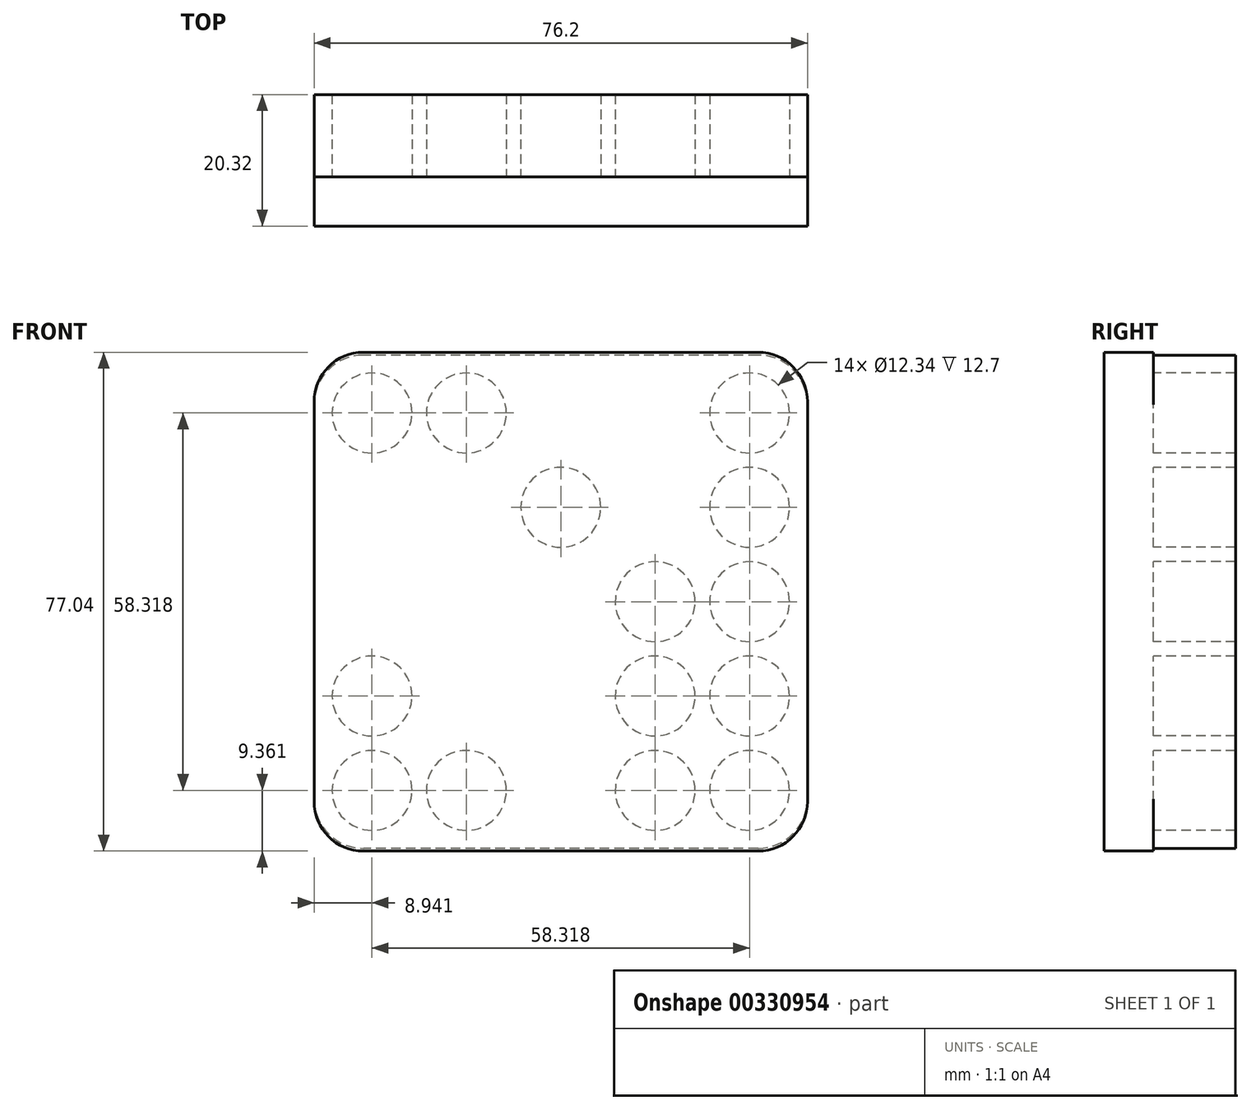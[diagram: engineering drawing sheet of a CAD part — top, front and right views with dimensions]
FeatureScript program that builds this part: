
annotation { "Feature Type Name" : "Feature", "Feature Type Description" : "" }
export const myFeature = defineFeature(function(context is Context, id is Id, definition is map)
    precondition{}
    {
        {
            var Q0;
            Q0=qCreatedBy(makeId("Front.planeOp"),FACE);
            var sketch = newSketch(context, id + "F0", { "sketchPlane" : qUnion([Q0])});
            skLineSegment(sketch, "E0.bottom", {"start": v(38.1, -38.1) * mm, "end": v(-38.1, -38.1) * mm});
            skLineSegment(sketch, "E0.top", {"start": v(38.1, 38.1) * mm, "end": v(-38.1, 38.1) * mm});
            skLineSegment(sketch, "E0.left", {"start": v(38.1, -38.1) * mm, "end": v(38.1, 38.1) * mm});
            skLineSegment(sketch, "E0.right", {"start": v(-38.1, -38.1) * mm, "end": v(-38.1, 38.1) * mm});
            skPoint(sketch, "E0.middle", {"position": v(0, 0) * mm});
            skLineSegment(sketch, "E1.left", {"start": v(38.1, -38.1) * mm, "end": v(38.1, -30.48) * mm});
            skSolve(sketch);
        }
        {
            var Q0;
            Q0=qSketchRegion(id+"F0",true);
            extrude(context, id + "F1", {"entities" : qUnion([Q0]), "depth" : 12.7 * mm});
        }
        {
            var Q0;
            Q0=makeQuery(id+"F1.opExtrude","CAP_FACE",FACE,{"disambiguationData":[OSD([sQuery(id+"F0.wireOp",EDGE,"E0.bottom"),sQuery(id+"F0.wireOp",EDGE,"E0.top"),sQuery(id+"F0.wireOp",EDGE,"E0.left"),sQuery(id+"F0.wireOp",EDGE,"E0.right"),sQuery(id+"F0.wireOp",EDGE,"jwXeI2Gn-2uBu-UpR7-ZfaP-BlmGfNdsuJBv.bottom"),sQuery(id+"F0.wireOp",EDGE,"jwXeI2Gn-2uBu-UpR7-ZfaP-BlmGfNdsuJBv.top"),sQuery(id+"F0.wireOp",EDGE,"jwXeI2Gn-2uBu-UpR7-ZfaP-BlmGfNdsuJBv.right"),sQuery(id+"F0.wireOp",EDGE,"E1.bottom"),sQuery(id+"F0.wireOp",EDGE,"E1.top"),sQuery(id+"F0.wireOp",EDGE,"E1.right"),sQuery(id+"F0.wireOp",EDGE,"Ah4uGkzg-DGqc-S60Q-QTGu-lLs24q3gFamp.bottom"),sQuery(id+"F0.wireOp",EDGE,"Ah4uGkzg-DGqc-S60Q-QTGu-lLs24q3gFamp.left"),sQuery(id+"F0.wireOp",EDGE,"Ah4uGkzg-DGqc-S60Q-QTGu-lLs24q3gFamp.right")])],"isStart":false});
            var sketch = newSketch(context, id + "F2", { "sketchPlane" : qUnion([Q0])});
            skLineSegment(sketch, "E2.bottom", {"start": v(0, 0) * mm, "end": v(14.58, 0) * mm});
            skLineSegment(sketch, "E2.top", {"start": v(0, 14.58) * mm, "end": v(14.58, 14.58) * mm});
            skLineSegment(sketch, "E2.left", {"start": v(0, 0) * mm, "end": v(0, 14.58) * mm});
            skLineSegment(sketch, "E2.right", {"start": v(14.58, 0) * mm, "end": v(14.58, 14.58) * mm});
            skLineSegment(sketch, "E3.top", {"start": v(0, 29.16) * mm, "end": v(14.58, 29.16) * mm});
            skLineSegment(sketch, "E3.left", {"start": v(0, 14.58) * mm, "end": v(0, 29.16) * mm});
            skLineSegment(sketch, "E3.right", {"start": v(14.58, 14.58) * mm, "end": v(14.58, 29.16) * mm});
            skLineSegment(sketch, "E4.top", {"start": v(0, -14.58) * mm, "end": v(14.58, -14.58) * mm});
            skLineSegment(sketch, "E4.left", {"start": v(0, 0) * mm, "end": v(0, -14.58) * mm});
            skLineSegment(sketch, "E4.right", {"start": v(14.58, 0) * mm, "end": v(14.58, -14.58) * mm});
            skLineSegment(sketch, "E5.bottom", {"start": v(0, 0) * mm, "end": v(-14.58, 0) * mm});
            skLineSegment(sketch, "E5.top", {"start": v(0, -14.58) * mm, "end": v(-14.58, -14.58) * mm});
            skLineSegment(sketch, "E5.right", {"start": v(-14.58, 0) * mm, "end": v(-14.58, -14.58) * mm});
            skLineSegment(sketch, "E6.bottom", {"start": v(0, 14.58) * mm, "end": v(-14.58, 14.58) * mm});
            skLineSegment(sketch, "E6.left", {"start": v(0, 14.58) * mm, "end": v(0, 0) * mm});
            skLineSegment(sketch, "E6.right", {"start": v(-14.58, 14.58) * mm, "end": v(-14.58, 0) * mm});
            skLineSegment(sketch, "E7.top", {"start": v(0, 29.16) * mm, "end": v(-14.58, 29.16) * mm});
            skLineSegment(sketch, "E7.right", {"start": v(-14.58, 14.58) * mm, "end": v(-14.58, 29.16) * mm});
            skLineSegment(sketch, "E8.bottom", {"start": v(-14.58, 14.58) * mm, "end": v(-29.16, 14.58) * mm});
            skLineSegment(sketch, "E8.top", {"start": v(-14.58, 29.16) * mm, "end": v(-29.16, 29.16) * mm});
            skLineSegment(sketch, "E8.right", {"start": v(-29.16, 14.58) * mm, "end": v(-29.16, 29.16) * mm});
            skLineSegment(sketch, "E9.top", {"start": v(-14.58, 0) * mm, "end": v(-29.16, 0) * mm});
            skLineSegment(sketch, "E9.right", {"start": v(-29.16, 14.58) * mm, "end": v(-29.16, 0) * mm});
            skLineSegment(sketch, "E10.bottom", {"start": v(-14.58, -14.58) * mm, "end": v(-29.16, -14.58) * mm});
            skLineSegment(sketch, "E10.left", {"start": v(-14.58, -14.58) * mm, "end": v(-14.58, 0) * mm});
            skLineSegment(sketch, "E10.right", {"start": v(-29.16, -14.58) * mm, "end": v(-29.16, 0) * mm});
            skLineSegment(sketch, "E11.bottom", {"start": v(14.58, -14.58) * mm, "end": v(29.16, -14.58) * mm});
            skLineSegment(sketch, "E11.top", {"start": v(14.58, 0) * mm, "end": v(29.16, 0) * mm});
            skLineSegment(sketch, "E11.left", {"start": v(14.58, -14.58) * mm, "end": v(14.58, 0) * mm});
            skLineSegment(sketch, "E11.right", {"start": v(29.16, -14.58) * mm, "end": v(29.16, 0) * mm});
            skLineSegment(sketch, "E12.top", {"start": v(14.58, 14.58) * mm, "end": v(29.16, 14.58) * mm});
            skLineSegment(sketch, "E12.right", {"start": v(29.16, 0) * mm, "end": v(29.16, 14.58) * mm});
            skLineSegment(sketch, "E13.top", {"start": v(14.58, 29.16) * mm, "end": v(29.16, 29.16) * mm});
            skLineSegment(sketch, "E13.right", {"start": v(29.16, 14.58) * mm, "end": v(29.16, 29.16) * mm});
            skLineSegment(sketch, "E14.top", {"start": v(14.58, -29.16) * mm, "end": v(29.16, -29.16) * mm});
            skLineSegment(sketch, "E14.left", {"start": v(14.58, -14.58) * mm, "end": v(14.58, -29.16) * mm});
            skLineSegment(sketch, "E14.right", {"start": v(29.16, -14.58) * mm, "end": v(29.16, -29.16) * mm});
            skLineSegment(sketch, "E15.bottom", {"start": v(14.58, -29.16) * mm, "end": v(0, -29.16) * mm});
            skLineSegment(sketch, "E15.top", {"start": v(14.58, -14.58) * mm, "end": v(0, -14.58) * mm});
            skLineSegment(sketch, "E15.left", {"start": v(14.58, -29.16) * mm, "end": v(14.58, -14.58) * mm});
            skLineSegment(sketch, "E15.right", {"start": v(0, -29.16) * mm, "end": v(0, -14.58) * mm});
            skLineSegment(sketch, "E16.bottom", {"start": v(0, -29.16) * mm, "end": v(-14.58, -29.16) * mm});
            skLineSegment(sketch, "E16.right", {"start": v(-14.58, -29.16) * mm, "end": v(-14.58, -14.58) * mm});
            skLineSegment(sketch, "E17.bottom", {"start": v(-14.58, -29.16) * mm, "end": v(-29.16, -29.16) * mm});
            skLineSegment(sketch, "E17.right", {"start": v(-29.16, -29.16) * mm, "end": v(-29.16, -14.58) * mm});
            skSolve(sketch);
        }
        {
            var Q0;
            Q0=sQuery(id+"F2.wireOp",VERTEX,"E8.top.end");
            var Q1;
            Q1=sQuery(id+"F2.wireOp",VERTEX,"E8.top.start");
            var Q2;
            Q2=sQuery(id+"F2.wireOp",VERTEX,"E3.left.end");
            var Q3;
            Q3=sQuery(id+"F2.wireOp",VERTEX,"E3.right.end");
            var Q4;
            Q4=sQuery(id+"F2.wireOp",VERTEX,"E13.right.end");
            var Q5;
            Q5=sQuery(id+"F2.wireOp",VERTEX,"E12.top.end");
            var Q6;
            Q6=sQuery(id+"F2.wireOp",VERTEX,"E11.right.end");
            var Q7;
            Q7=sQuery(id+"F2.wireOp",VERTEX,"E11.bottom.end");
            var Q8;
            Q8=sQuery(id+"F2.wireOp",VERTEX,"E14.top.end");
            var Q9;
            Q9=sQuery(id+"F2.wireOp",VERTEX,"E14.top.start");
            var Q10;
            Q10=sQuery(id+"F2.wireOp",VERTEX,"E14.left.start");
            var Q11;
            Q11=sQuery(id+"F2.wireOp",VERTEX,"E11.left.end");
            var Q12;
            Q12=sQuery(id+"F2.wireOp",VERTEX,"E2.top.end");
            var Q13;
            Q13=sQuery(id+"F2.wireOp",VERTEX,"E6.left.start");
            var Q14;
            Q14=sQuery(id+"F2.wireOp",VERTEX,"E2.bottom.start");
            var Q15;
            Q15=sQuery(id+"F2.wireOp",VERTEX,"E4.left.end");
            var Q16;
            Q16=sQuery(id+"F2.wireOp",VERTEX,"E15.right.start");
            var Q17;
            Q17=sQuery(id+"F2.wireOp",VERTEX,"E16.right.start");
            var Q18;
            Q18=sQuery(id+"F2.wireOp",VERTEX,"E16.right.end");
            var Q19;
            Q19=sQuery(id+"F2.wireOp",VERTEX,"E6.right.end");
            var Q20;
            Q20=sQuery(id+"F2.wireOp",VERTEX,"E7.right.start");
            var Q21;
            Q21=sQuery(id+"F2.wireOp",VERTEX,"E8.bottom.end");
            var Q22;
            Q22=sQuery(id+"F2.wireOp",VERTEX,"E9.top.end");
            var Q23;
            Q23=sQuery(id+"F2.wireOp",VERTEX,"E17.right.end");
            var Q24;
            Q24=sQuery(id+"F2.wireOp",VERTEX,"E17.bottom.end");
            var Q25;
            Q25=makeQuery(id+"F1.opExtrude","SWEPT_BODY",BODY,{"disambiguationData":[OSD([sQuery(id+"F0.wireOp",EDGE,"E0.bottom"),sQuery(id+"F0.wireOp",EDGE,"E0.top"),sQuery(id+"F0.wireOp",EDGE,"E0.left"),sQuery(id+"F0.wireOp",EDGE,"E0.right"),sQuery(id+"F0.wireOp",EDGE,"jwXeI2Gn-2uBu-UpR7-ZfaP-BlmGfNdsuJBv.bottom"),sQuery(id+"F0.wireOp",EDGE,"jwXeI2Gn-2uBu-UpR7-ZfaP-BlmGfNdsuJBv.top"),sQuery(id+"F0.wireOp",EDGE,"jwXeI2Gn-2uBu-UpR7-ZfaP-BlmGfNdsuJBv.right"),sQuery(id+"F0.wireOp",EDGE,"E1.bottom"),sQuery(id+"F0.wireOp",EDGE,"E1.top"),sQuery(id+"F0.wireOp",EDGE,"E1.right"),sQuery(id+"F0.wireOp",EDGE,"Ah4uGkzg-DGqc-S60Q-QTGu-lLs24q3gFamp.bottom"),sQuery(id+"F0.wireOp",EDGE,"Ah4uGkzg-DGqc-S60Q-QTGu-lLs24q3gFamp.left"),sQuery(id+"F0.wireOp",EDGE,"Ah4uGkzg-DGqc-S60Q-QTGu-lLs24q3gFamp.right")])]});
            hole(context, id + "F3", {"style" : HoleStyle.SIMPLE, "endStyle" : HoleEndStyle.THROUGH, "holeDiameter" : 12.34 * mm, "tappedDepth" : 12.7 * mm, "tapClearance" : 3, "locations" : qUnion([Q0, Q1, Q2, Q3, Q4, Q5, Q6, Q7, Q8, Q9, Q10, Q11, Q12, Q13, Q14, Q15, Q16, Q17, Q18, Q19, Q20, Q21, Q22, Q23, Q24]), "scope" : qUnion([Q25])});
        }
        {
            var Q0;
            Q0=makeQuery(id+"F1.opExtrude","SWEPT_EDGE",EDGE,{"disambiguationData":[OSD([sQuery(id+"F0.wireOp",EDGE,"Ah4uGkzg-DGqc-S60Q-QTGu-lLs24q3gFamp.bottom"),sQuery(id+"F0.wireOp",EDGE,"Ah4uGkzg-DGqc-S60Q-QTGu-lLs24q3gFamp.right")])]});
            var Q1;
            Q1=makeQuery(id+"F1.opExtrude","SWEPT_EDGE",EDGE,{"disambiguationData":[OSD([sQuery(id+"F0.wireOp",EDGE,"Ah4uGkzg-DGqc-S60Q-QTGu-lLs24q3gFamp.bottom"),sQuery(id+"F0.wireOp",EDGE,"Ah4uGkzg-DGqc-S60Q-QTGu-lLs24q3gFamp.left")])]});
            var Q2;
            Q2=makeQuery(id+"F1.opExtrude","SWEPT_EDGE",EDGE,{"disambiguationData":[OSD([sQuery(id+"F0.wireOp",EDGE,"E0.top"),sQuery(id+"F0.wireOp",EDGE,"E0.right")])]});
            var Q3;
            Q3=makeQuery(id+"F1.opExtrude","SWEPT_EDGE",EDGE,{"disambiguationData":[OSD([sQuery(id+"F0.wireOp",EDGE,"E0.top"),sQuery(id+"F0.wireOp",EDGE,"E0.left")])]});
            var Q4;
            Q4=makeQuery(id+"F1.opExtrude","SWEPT_EDGE",EDGE,{"disambiguationData":[OSD([sQuery(id+"F0.wireOp",EDGE,"E1.top"),sQuery(id+"F0.wireOp",EDGE,"E1.right")])]});
            var Q5;
            Q5=makeQuery(id+"F1.opExtrude","SWEPT_EDGE",EDGE,{"disambiguationData":[OSD([sQuery(id+"F0.wireOp",EDGE,"jwXeI2Gn-2uBu-UpR7-ZfaP-BlmGfNdsuJBv.top"),sQuery(id+"F0.wireOp",EDGE,"jwXeI2Gn-2uBu-UpR7-ZfaP-BlmGfNdsuJBv.right")])]});
            var Q6;
            Q6=makeQuery(id+"F1.opExtrude","SWEPT_EDGE",EDGE,{"disambiguationData":[OSD([sQuery(id+"F0.wireOp",EDGE,"E0.bottom"),sQuery(id+"F0.wireOp",EDGE,"E1.left")])]});
            var Q7;
            Q7=makeQuery(id+"F1.opExtrude","SWEPT_EDGE",EDGE,{"disambiguationData":[OSD([sQuery(id+"F0.wireOp",EDGE,"E0.bottom"),sQuery(id+"F0.wireOp",EDGE,"E0.right")])]});
            fillet(context, id + "F4", {"entities" : qUnion([Q0, Q1, Q2, Q3, Q4, Q5, Q6, Q7]), "radius" : 7.62 * mm, "tangentPropagation" : true, "allowEdgeOverflow" : false});
        }
        {
            var Q0;
            Q0=makeQuery(id+"F1.opExtrude","CAP_FACE",FACE,{"disambiguationData":[OSD([sQuery(id+"F0.wireOp",EDGE,"E0.bottom"),sQuery(id+"F0.wireOp",EDGE,"E0.top"),sQuery(id+"F0.wireOp",EDGE,"E0.left"),sQuery(id+"F0.wireOp",EDGE,"E0.right"),sQuery(id+"F0.wireOp",EDGE,"E1.left")])],"isStart":false});
            var sketch = newSketch(context, id + "F5", { "sketchPlane" : qUnion([Q0])});
            skLineSegment(sketch, "E18.bottom", {"start": v(38.1, -38.52) * mm, "end": v(-38.1, -38.52) * mm});
            skLineSegment(sketch, "E18.top", {"start": v(38.1, 38.52) * mm, "end": v(-38.1, 38.52) * mm});
            skLineSegment(sketch, "E18.left", {"start": v(38.1, -38.52) * mm, "end": v(38.1, 38.52) * mm});
            skLineSegment(sketch, "E18.right", {"start": v(-38.1, -38.52) * mm, "end": v(-38.1, 38.52) * mm});
            skPoint(sketch, "E18.middle", {"position": v(0, 0) * mm});
            skSolve(sketch);
        }
        {
            var Q0;
            Q0=qSketchRegion(id+"F5",true);
            extrude(context, id + "F6", {"entities" : qUnion([Q0]), "operationType" : NewBodyOperationType.ADD, "depth" : 7.62 * mm});
        }
        {
            var Q0;
            Q0=makeQuery(id+"F6.opExtrude","SWEPT_EDGE",EDGE,{"disambiguationData":[OSD([sQuery(id+"F5.wireOp",EDGE,"E18.top"),sQuery(id+"F5.wireOp",EDGE,"E18.right")])]});
            var Q1;
            Q1=makeQuery(id+"F6.opExtrude","SWEPT_EDGE",EDGE,{"disambiguationData":[OSD([sQuery(id+"F5.wireOp",EDGE,"E18.top"),sQuery(id+"F5.wireOp",EDGE,"E18.left")])]});
            var Q2;
            Q2=makeQuery(id+"F6.opExtrude","SWEPT_EDGE",EDGE,{"disambiguationData":[OSD([sQuery(id+"F5.wireOp",EDGE,"E18.bottom"),sQuery(id+"F5.wireOp",EDGE,"E18.left")])]});
            var Q3;
            Q3=makeQuery(id+"F6.opExtrude","SWEPT_EDGE",EDGE,{"disambiguationData":[OSD([sQuery(id+"F5.wireOp",EDGE,"E18.bottom"),sQuery(id+"F5.wireOp",EDGE,"E18.right")])]});
            fillet(context, id + "F7", {"entities" : qUnion([Q0, Q1, Q2, Q3]), "radius" : 7.62 * mm, "tangentPropagation" : true, "allowEdgeOverflow" : false});
        }
    });
